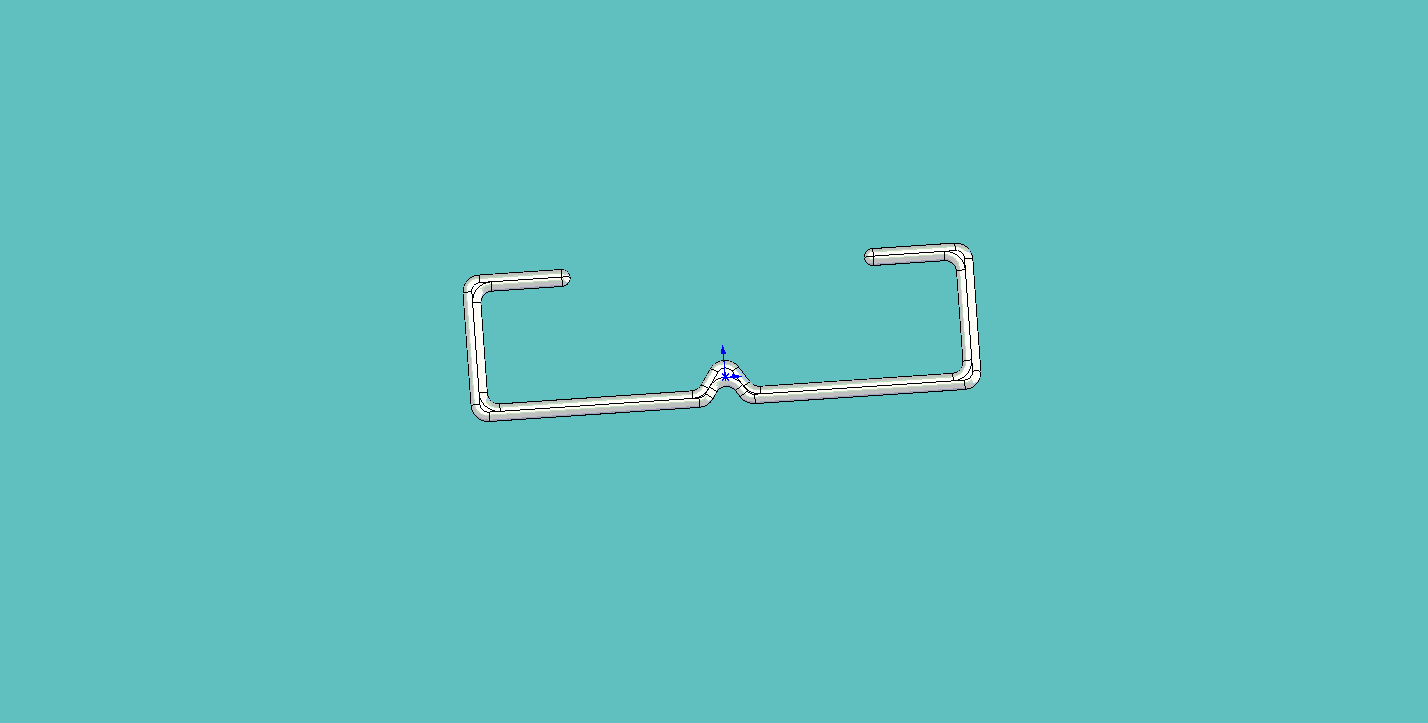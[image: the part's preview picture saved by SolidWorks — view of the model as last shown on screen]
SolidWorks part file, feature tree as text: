
SOLIDWORKS PART (.sldprt)
format: sldprt  version: not decoded by parser v0  size: 233,472 bytes
history: native  units: mm
features: plane x3, fillet x3, material x1, sketch x1, extrude x1 (+10 scaffold rows collapsed)
feature tree (19):
  scaffold x10  (default folders/planes/origin — collapsed)
  material  "Matériau <non spécifié>"
  plane  "Plan de face"
  plane  "Plan de dessus"
  plane  "Plan de droite"
  sketch  "Esquisse1"  dims[c1.D6=0.4mm c1.D7=0.6mm c1.D8=0.6mm c1.D10=0.4mm c1.D1=3.8mm c1.D2=5.2mm c1.D3=0.6mm c1.D4=9.0mm c1.D5=9.0mm c2.D8=1.0mm c2.D9=2.4mm]
  extrude  "Extrusion1"  Depth=0.6mm
  fillet  "Congé1"  Radius=0.6mm
  fillet  "Congé2"  Radius=0.3mm
  fillet  "Congé3"  Radius=0.3mm
decode coverage: 5 of 5 modeling features carry decoded parameters
note: suppression state not decoded; provenance and decode notes live in map.json
